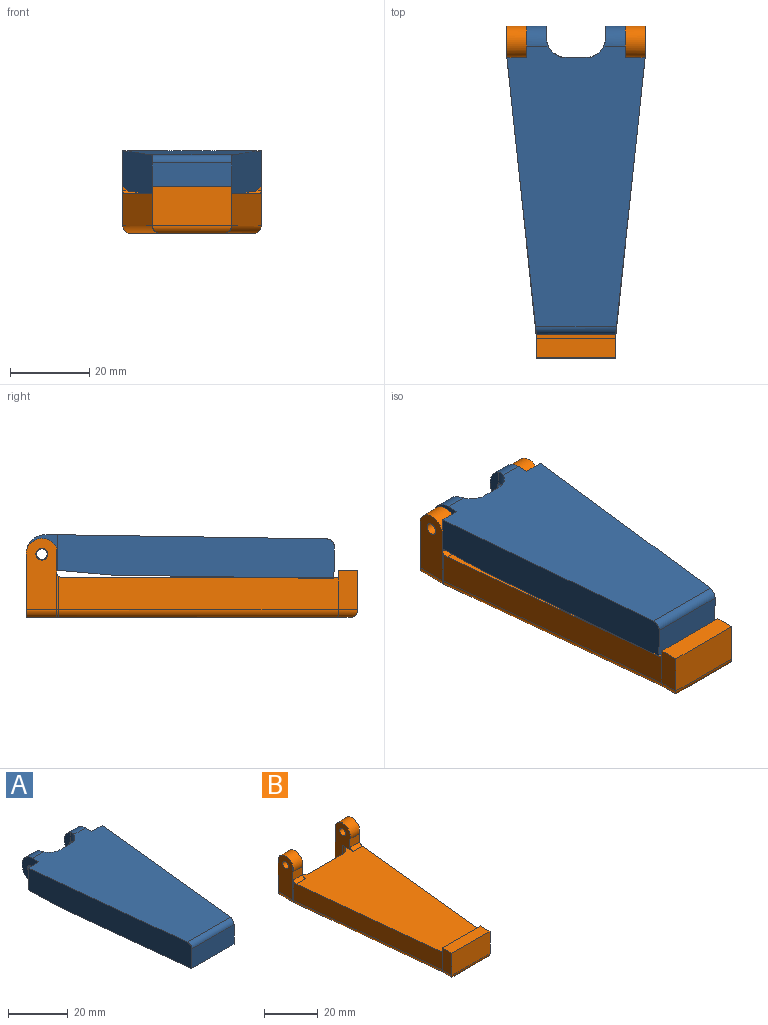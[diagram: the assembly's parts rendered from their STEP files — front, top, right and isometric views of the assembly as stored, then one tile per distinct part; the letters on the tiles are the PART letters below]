
ASSEMBLY  parts=2 mates=1
PART A: 24 faces, bbox 35.1x78.1x10.1 mm
  f0: plane 9x5mm, normal (0,1,0), area 45mm2, adj f4,f10,f15,f22
  f1: plane 9x5mm, normal (0,1,0), area 45mm2, adj f8,f9,f15,f22
  f2: plane 9x5mm, normal (0,1,0), area 45mm2, adj f3,f13,f15,f22
  f3: plane 70.09x10.09mm, normal (-0.99,-0.11,0), area 696.2mm2, adj f2,f7,f14,f15,f20,f22
  f4: plane 70.09x10.09mm, normal (0.99,-0.11,0), area 696.2mm2, adj f0,f7,f14,f15,f20,f22
  f5: plane 7x2mm, normal (0,0,-1), area 12.1mm2, adj f9,f13,f18,f23
  f6: plane 7x2mm, normal (0,0,-1), area 12.1mm2, adj f8,f10,f19,f21
  f7: plane 56.11x32.02mm, normal (0,0,-1), area 1459.7mm2, adj f3,f4,f14,f22
  f8: cylinder r=5mm len=10mm, axis (0,0,1), area 69.7mm2, adj f1,f6,f11,f15,f17,f19,f21
  f9: cylinder r=5mm len=10mm, axis (0,0,-1), area 69.7mm2, adj f1,f5,f12,f15,f16,f18,f23
  f10: plane 10x8mm, normal (1,0,0), area 62.8mm2, adj f0,f6,f15,f17,f19,f21
  f11: plane 9.17x3mm, normal (-1,0,0), area 19.4mm2, adj f8,f17,f19
  f12: plane 9.17x3mm, normal (1,0,0), area 19.4mm2, adj f9,f16,f18
  f13: plane 10x8mm, normal (-1,0,0), area 62.8mm2, adj f2,f5,f15,f16,f18,f23
  f14: plane 20x8mm, normal (0,-1,0), area 160mm2, adj f3,f4,f7,f20
  f15: plane 71x35mm, normal (0,0,1), area 1924.8mm2, adj f0,f1,f2,f3,f4,f8,f9,f10
  f16: cylinder r=1.35mm len=5.59mm, axis (1,0,0), area 44.1mm2, adj f9,f12,f13
  f17: cylinder r=1.35mm len=5.59mm, axis (1,0,0), area 44.1mm2, adj f8,f10,f11
  f18: cylinder r=5mm len=10mm, axis (1,0,0), area 79.1mm2, adj f5,f9,f12,f13,f15
  f19: cylinder r=5mm len=10mm, axis (1,0,0), area 79.1mm2, adj f6,f8,f10,f11,f15
  f20: cylinder r=2mm len=20.43mm, axis (-1,0,0), area 63.5mm2, adj f3,f4,f14,f15
  f21: cylinder r=1mm len=10mm, axis (-1,0,0), area 12.1mm2, adj f6,f8,f10,f22
  f22: plane 35x13.89mm, normal (0,0.07,-1), area 466.5mm2, adj f0,f1,f2,f3,f4,f7,f21,f23
  f23: cylinder r=1mm len=10mm, axis (-1,0,0), area 12.1mm2, adj f5,f9,f13,f22
PART B: 39 faces, bbox 35x84x20 mm
  f0: plane 70.8x8.48mm, normal (0.99,-0.11,0), area 569.7mm2, adj f5,f8,f24,f32,f35
  f1: plane 70.8x8.48mm, normal (-0.99,-0.11,0), area 569.7mm2, adj f5,f6,f21,f28,f37
  f2: cylinder r=4mm len=2.56mm, axis (0,0,1), area 0.4mm2, adj f16,f22
  f3: cylinder r=4mm len=2.56mm, axis (0,0,-1), area 0.3mm2, adj f13,f23
  f4: plane 17x10mm, normal (0,1,0), area 170mm2, adj f5,f9,f20,f25
  f5: plane 75x34.68mm, normal (0,0,1), area 1944.6mm2, adj f0,f1,f4,f10,f12,f15,f20,f25
  f6: plane 10x5mm, normal (-1,0,0), area 50mm2, adj f1,f7,f10,f11,f29
  f7: plane 20x10mm, normal (0,-1,0), area 200mm2, adj f6,f8,f11,f30
  f8: plane 10x5mm, normal (1,0,0), area 50mm2, adj f0,f7,f10,f11,f31
  f9: plane 82x31mm, normal (0,0,-1), area 1769.8mm2, adj f4,f12,f14,f15,f17,f20,f25,f26
  f10: plane 20x2mm, normal (0,1,0), area 40mm2, adj f5,f6,f8,f11
  f11: plane 20x5mm, normal (0,0,1), area 100mm2, adj f6,f7,f8,f10
  f12: plane 20x9.5mm, normal (-1,0,0), area 105.5mm2, adj f5,f9,f14,f19,f23,f25,f35,f36
  f13: plane 18x7.79mm, normal (1,0,0), area 126.9mm2, adj f3,f14,f19,f23,f24,f34,f36
  f14: plane 16x5mm, normal (0,1,0), area 79.1mm2, adj f9,f12,f13,f23,f34
  f15: plane 20x9.5mm, normal (1,0,0), area 105.5mm2, adj f5,f9,f17,f18,f20,f22,f37,f38
  f16: plane 18x7.79mm, normal (-1,0,0), area 126.9mm2, adj f2,f17,f18,f21,f22,f26,f38
  f17: plane 16x5mm, normal (0,1,0), area 79.1mm2, adj f9,f15,f16,f22,f26
  f18: cylinder r=1.5mm len=5mm, axis (1,0,0), area 47.1mm2, adj f15,f16
  f19: cylinder r=1.5mm len=5mm, axis (1,0,0), area 47.1mm2, adj f12,f13
  f20: cylinder r=4mm len=10mm, axis (0,0,-1), area 62.8mm2, adj f4,f5,f9,f15
  f21: cylinder r=4mm len=8.96mm, axis (0,0,1), area 3.7mm2, adj f1,f16,f27,f37
  f22: cylinder r=4mm len=8mm, axis (-1,0,0), area 69.4mm2, adj f2,f15,f16,f17,f38
  f23: cylinder r=4mm len=8mm, axis (-1,0,0), area 69.3mm2, adj f3,f12,f13,f14,f36
  f24: cylinder r=4mm len=8.96mm, axis (0,0,-1), area 3.7mm2, adj f0,f13,f33,f35
  f25: cylinder r=4mm len=10mm, axis (0,0,1), area 62.8mm2, adj f4,f5,f9,f12
  f26: cylinder r=2mm len=7.79mm, axis (0,-1,0), area 24.5mm2, adj f9,f16,f17,f27
  f27: torus R=2mm, axis (0,0,1), area 1.1mm2, adj f9,f21,f26,f28
  f28: cylinder r=2mm len=71.11mm, axis (0.11,-0.99,0), area 223.8mm2, adj f1,f9,f27,f29
  f29: cylinder r=2mm len=5.11mm, axis (0,-1,0), area 12.7mm2, adj f6,f9,f28,f30
  f30: cylinder r=2mm len=20mm, axis (1,0,0), area 56.5mm2, adj f7,f9,f29,f31
  f31: cylinder r=2mm len=5.11mm, axis (0,1,0), area 12.7mm2, adj f8,f9,f30,f32
  f32: cylinder r=2mm len=71.11mm, axis (0.11,0.99,0), area 223.8mm2, adj f0,f9,f31,f33
  f33: torus R=2mm, axis (0,0,1), area 1.1mm2, adj f9,f24,f32,f34
  f34: cylinder r=2mm len=7.79mm, axis (0,1,0), area 24.5mm2, adj f9,f13,f14,f33
  f35: cylinder r=2mm len=5mm, axis (1,0,0), area 10.1mm2, adj f0,f5,f12,f24,f36
  f36: plane 5x3.76mm, normal (0,-1,0), area 18.8mm2, adj f12,f13,f23,f35
  f37: cylinder r=2mm len=5mm, axis (1,0,0), area 10.1mm2, adj f1,f5,f15,f21,f38
  f38: plane 5x3.76mm, normal (0,-1,0), area 18.8mm2, adj f15,f16,f22,f37
PLACE A rot(axis=(1,0,0),0.9deg) t=(0,0.08,10.94)mm
PLACE B at identity fixed
MATE revolute A.f16 <-> B.f22  axis (1,0,0) through (30,4,16)mm
